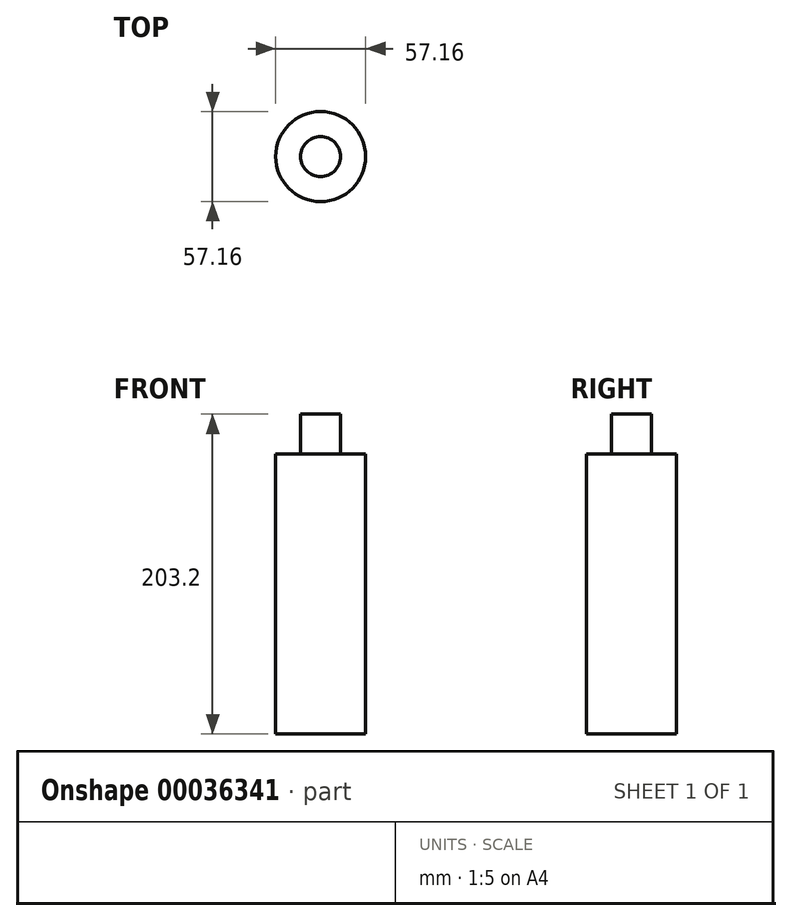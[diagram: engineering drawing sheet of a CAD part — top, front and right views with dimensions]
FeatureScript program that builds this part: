
annotation { "Feature Type Name" : "Feature", "Feature Type Description" : "" }
export const myFeature = defineFeature(function(context is Context, id is Id, definition is map)
    precondition{}
    {
        {
            var Q0;
            Q0=qCreatedBy(makeId("Top.planeOp"),FACE);
            var sketch = newSketch(context, id + "F0", { "sketchPlane" : qUnion([Q0])});
            skCircle(sketch, "E0", {"center": v(0, 0) * mm, "radius": 28.58 * mm});
            skSolve(sketch);
        }
        {
            var Q0;
            Q0 = qSketchRegion(id + "F0", true);
            var Q1;
            Q1=sQuery(id+"F0.wireOp",EDGE,"E0");
            extrude(context, id + "F1", {"entities" : qUnion([Q0]), "surfaceEntities" : qUnion([Q1]), "depth" : 177.8 * mm});
        }
        {
            var Q0;
            Q0=makeQuery(id+"F1.opExtrude","CAP_FACE",FACE,{"disambiguationData":[OSD([sQuery(id+"F0.wireOp",EDGE,"E0")])],"isStart":false});
            var sketch = newSketch(context, id + "F2", { "sketchPlane" : qUnion([Q0])});
            skCircle(sketch, "E1", {"center": v(0, 0) * mm, "radius": 12.7 * mm});
            skSolve(sketch);
        }
        {
            var Q0;
            Q0=makeQuery(id+"F2.imprint","IMPRINT",FACE,{"disambiguationData":[TD([[makeQuery(id+"F2.imprint","IMPRINT",EDGE,{"derivedFrom":sQuery(id+"F2.wireOp",EDGE,"E1")}),1.0]])]});
            extrude(context, id + "F3", {"entities" : qUnion([Q0]), "operationType" : NewBodyOperationType.ADD, "depth" : 25.4 * mm});
        }
    });
